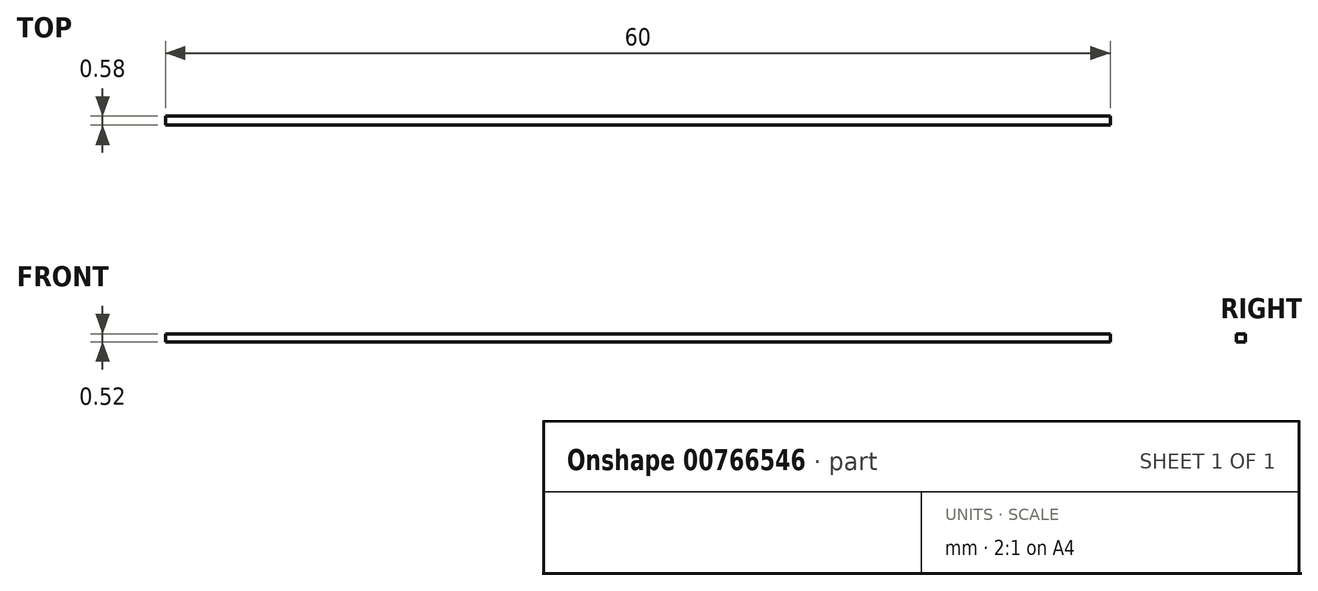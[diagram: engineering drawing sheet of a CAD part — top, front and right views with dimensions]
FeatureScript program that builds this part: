
annotation { "Feature Type Name" : "Feature", "Feature Type Description" : "" }
export const myFeature = defineFeature(function(context is Context, id is Id, definition is map)
    precondition{}
    {
        {
            var Q0;
            Q0=qCreatedBy(makeId("Right.planeOp"),FACE);
            var sketch = newSketch(context, id + "F0", { "sketchPlane" : qUnion([Q0])});
            skLineSegment(sketch, "E0.bottom", {"start": v(0.29, 0.26) * mm, "end": v(-0.29, 0.26) * mm});
            skLineSegment(sketch, "E0.top", {"start": v(0.29, -0.26) * mm, "end": v(-0.29, -0.26) * mm});
            skLineSegment(sketch, "E0.left", {"start": v(0.29, 0.26) * mm, "end": v(0.29, -0.26) * mm});
            skLineSegment(sketch, "E0.right", {"start": v(-0.29, 0.26) * mm, "end": v(-0.29, -0.26) * mm});
            skPoint(sketch, "E0.middle", {"position": v(0, 0) * mm});
            skSolve(sketch);
        }
        {
            var Q0;
            Q0=makeQuery(id+"F0.imprint","IMPRINT",FACE,{"disambiguationData":[TD([[makeQuery(id+"F0.imprint","IMPRINT",EDGE,{"derivedFrom":sQuery(id+"F0.wireOp",EDGE,"E0.bottom")}),1.0]])]});
            extrude(context, id + "F1", {"entities" : qUnion([Q0]), "depth" : 60 * mm, "offsetDistance" : 25 * mm});
        }
    });
